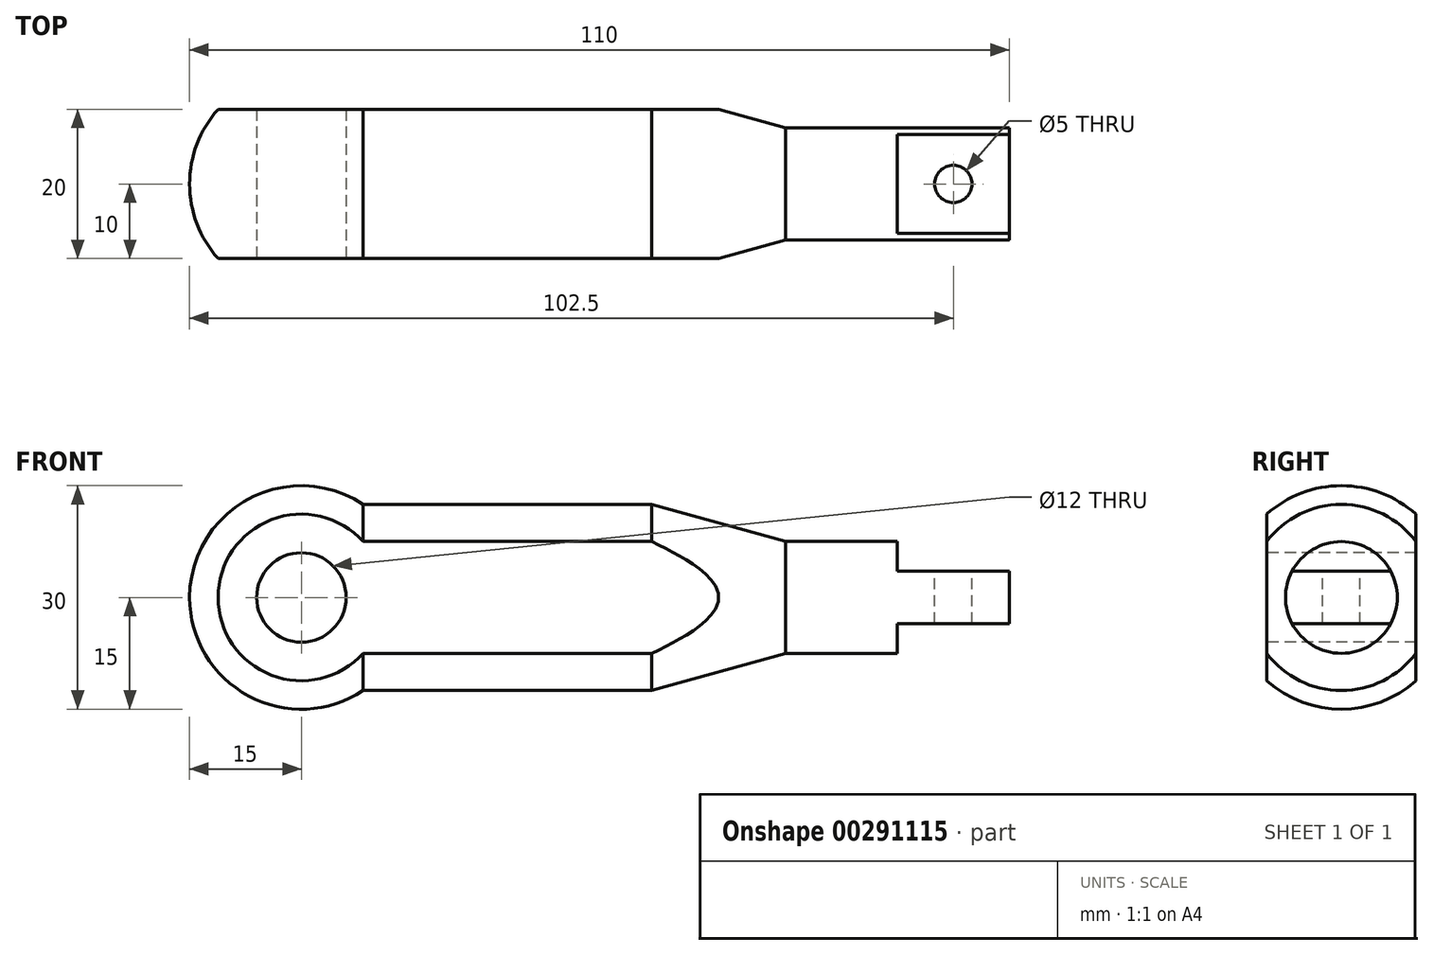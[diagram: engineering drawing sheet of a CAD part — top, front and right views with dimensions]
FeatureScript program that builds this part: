
annotation { "Feature Type Name" : "Feature", "Feature Type Description" : "" }
export const myFeature = defineFeature(function(context is Context, id is Id, definition is map)
    precondition{}
    {
        {
            var Q0;
            Q0=qCreatedBy(makeId("Front.planeOp"),FACE);
            var sketch = newSketch(context, id + "F0", { "sketchPlane" : qUnion([Q0])});
            skLineSegment(sketch, "E0", {"start": v(0, 0) * mm, "end": v(97.01, 0) * mm, "construction": true});
            skArc(sketch, "E1", {"start": v(-15, 0) * mm, "mid": v(-7.1, 13.22) * mm, "end": v(8.3, 12.5) * mm});
            skLineSegment(sketch, "E2", {"start": v(8.3, 12.5) * mm, "end": v(47, 12.5) * mm});
            skLineSegment(sketch, "E3", {"start": v(47, 12.5) * mm, "end": v(65, 7.5) * mm});
            skLineSegment(sketch, "E4", {"start": v(65, 7.5) * mm, "end": v(95, 7.5) * mm});
            skLineSegment(sketch, "E5", {"start": v(95, 7.5) * mm, "end": v(95, 0) * mm});
            skLineSegment(sketch, "E6", {"start": v(95, 0) * mm, "end": v(-15, 0) * mm});
            skSolve(sketch);
        }
        {
            var Q0;
            Q0 = qSketchRegion(id + "F0", true);
            var Q1;
            Q1=sQuery(id+"F0.wireOp",EDGE,"E6");
            revolve(context, id + "F1", {"entities" : qUnion([Q0]), "axis" : qUnion([Q1]), "revolveType" : RevolveType.FULL});
        }
        {
            var Q0;
            Q0=qCreatedBy(makeId("Front.planeOp"),FACE);
            var sketch = newSketch(context, id + "F2", { "sketchPlane" : qUnion([Q0])});
            skLineSegment(sketch, "E7.top", {"start": v(80, 3.5) * mm, "end": v(95, 3.5) * mm});
            skLineSegment(sketch, "E7.left", {"start": v(80, 7.5) * mm, "end": v(80, 3.5) * mm});
            skLineSegment(sketch, "E8", {"start": v(95, -7.5) * mm, "end": v(80, -7.5) * mm});
            skLineSegment(sketch, "E9", {"start": v(80, 7.5) * mm, "end": v(95, 7.5) * mm});
            skLineSegment(sketch, "E10", {"start": v(95, 7.5) * mm, "end": v(95, 3.5) * mm});
            skLineSegment(sketch, "E11", {"start": v(68.47, 0) * mm, "end": v(123.21, 0) * mm, "construction": true});
            skLineSegment(sketch, "E12.MirrorCS", {"start": v(80, -7.5) * mm, "end": v(95, -7.5) * mm});
            skLineSegment(sketch, "E13.MirrorCS", {"start": v(95, -7.5) * mm, "end": v(95, -3.5) * mm});
            skLineSegment(sketch, "E14.MirrorCS", {"start": v(80, -7.5) * mm, "end": v(80, -3.5) * mm});
            skLineSegment(sketch, "E15.MirrorCS", {"start": v(80, -3.5) * mm, "end": v(95, -3.5) * mm});
            skSolve(sketch);
        }
        {
            var Q0;
            Q0 = qSketchRegion(id + "F2", true);
            extrude(context, id + "F3", {"entities" : qUnion([Q0]), "operationType" : NewBodyOperationType.REMOVE, "endBound" : BoundingType.THROUGH_ALL, "depth" : 25 * mm, "hasSecondDirection" : true, "secondDirectionBound" : SecondDirectionBoundingType.THROUGH_ALL, "secondDirectionOppositeDirection" : true, "secondDirectionDepth" : 25 * mm});
        }
        {
            var Q0;
            Q0=makeQuery(id+"F1.opRevolve","SWEPT_FACE",FACE,{"disambiguationData":[OSD([sQuery(id+"F0.wireOp",EDGE,"E5")])]});
            var sketch = newSketch(context, id + "F4", { "sketchPlane" : qUnion([Q0])});
            skLineSegment(sketch, "E16", {"start": v(-10, 11.18) * mm, "end": v(-10, -11.18) * mm});
            skArc(sketch, "E17", {"start": v(-10, 11.18) * mm, "mid": v(-15, 0) * mm, "end": v(-10, -11.18) * mm});
            skLineSegment(sketch, "E18", {"start": v(10, 11.18) * mm, "end": v(10, -11.18) * mm});
            skLineSegment(sketch, "E19", {"start": v(0, 0) * mm, "end": v(0, 36.95) * mm, "construction": true});
            skArc(sketch, "E20.trimOffspring", {"start": v(10, -11.18) * mm, "mid": v(15, 0) * mm, "end": v(10, 11.18) * mm});
            skSolve(sketch);
        }
        {
            var Q0;
            Q0 = qSketchRegion(id + "F4", true);
            extrude(context, id + "F5", {"entities" : qUnion([Q0]), "operationType" : NewBodyOperationType.REMOVE, "endBound" : BoundingType.THROUGH_ALL, "oppositeDirection" : true, "depth" : 25 * mm});
        }
        {
            var Q0;
            Q0=qCreatedBy(makeId("Front.planeOp"),FACE);
            var sketch = newSketch(context, id + "F6", { "sketchPlane" : qUnion([Q0])});
            skCircle(sketch, "E21", {"center": v(0, 0) * mm, "radius": 6 * mm});
            skSolve(sketch);
        }
        {
            var Q0;
            Q0 = qSketchRegion(id + "F6", true);
            extrude(context, id + "F7", {"entities" : qUnion([Q0]), "operationType" : NewBodyOperationType.REMOVE, "endBound" : BoundingType.THROUGH_ALL, "oppositeDirection" : true, "depth" : 25 * mm, "hasSecondDirection" : true, "secondDirectionBound" : SecondDirectionBoundingType.THROUGH_ALL, "secondDirectionOppositeDirection" : false, "secondDirectionDepth" : 25 * mm});
        }
        {
            var Q0;
            Q0=makeQuery(id+"F3.boolean.opBoolean","COPY",FACE,{"derivedFrom":makeQuery(id+"F3.opExtrude","SWEPT_FACE",FACE,{"disambiguationData":[OSD([sQuery(id+"F2.wireOp",EDGE,"E7.top")])]})});
            var sketch = newSketch(context, id + "F8", { "sketchPlane" : qUnion([Q0])});
            skCircle(sketch, "E22", {"center": v(87.5, 0) * mm, "radius": 2.5 * mm});
            skSolve(sketch);
        }
        {
            var Q0;
            Q0 = qSketchRegion(id + "F8", true);
            extrude(context, id + "F9", {"entities" : qUnion([Q0]), "operationType" : NewBodyOperationType.REMOVE, "endBound" : BoundingType.THROUGH_ALL, "oppositeDirection" : true, "depth" : 25 * mm});
        }
    });
